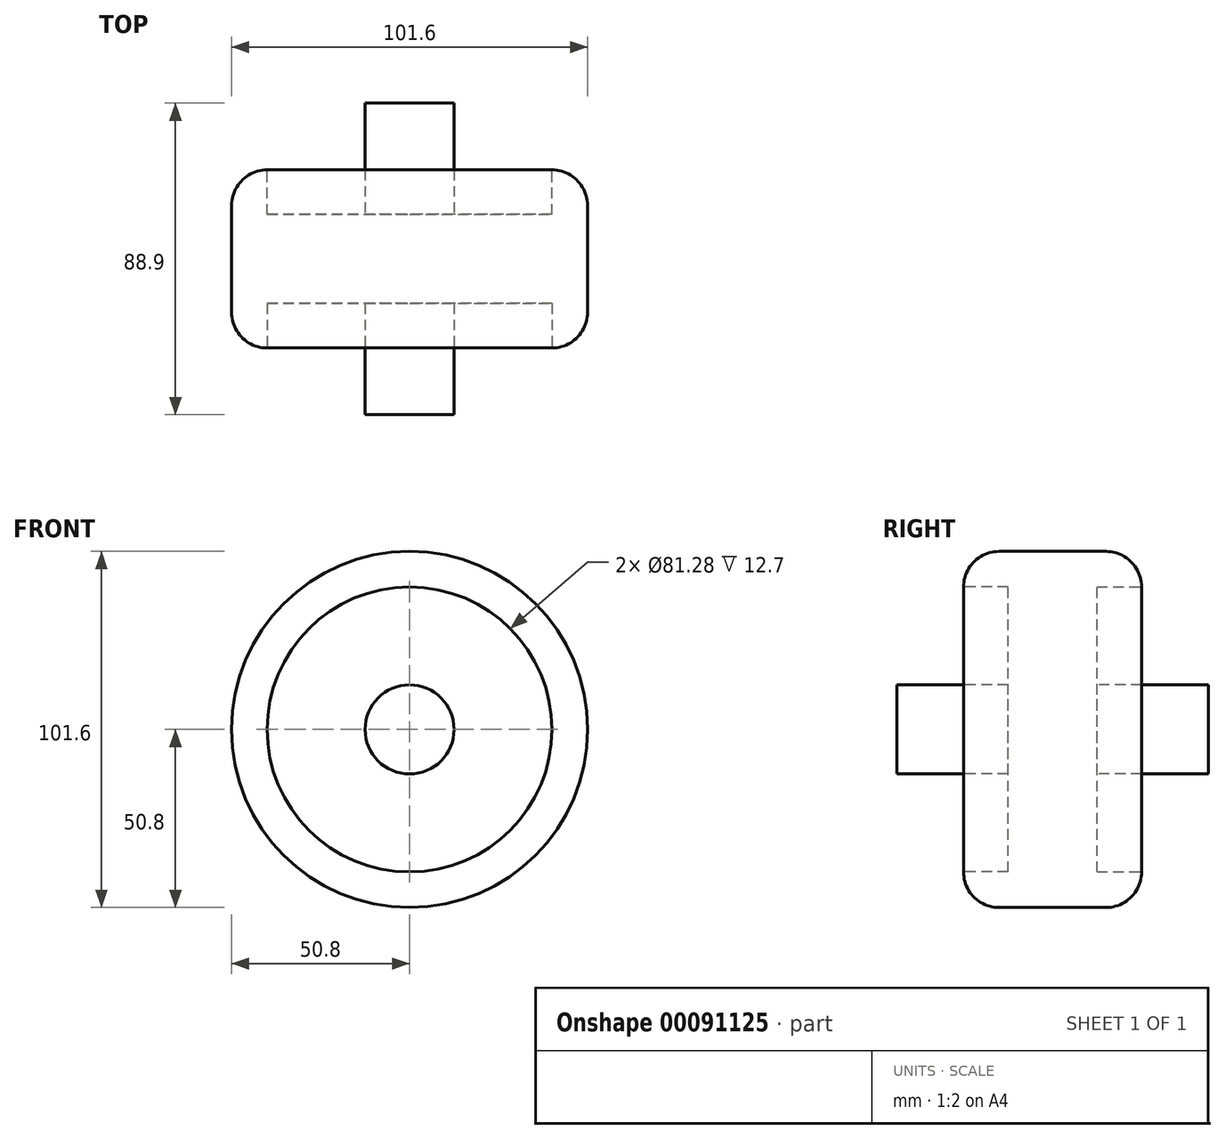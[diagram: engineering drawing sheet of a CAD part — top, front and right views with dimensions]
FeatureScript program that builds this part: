
annotation { "Feature Type Name" : "Feature", "Feature Type Description" : "" }
export const myFeature = defineFeature(function(context is Context, id is Id, definition is map)
    precondition{}
    {
        {
            var Q0;
            Q0=qCreatedBy(makeId("Front.planeOp"),FACE);
            var sketch = newSketch(context, id + "F0", { "sketchPlane" : qUnion([Q0])});
            skCircle(sketch, "E0", {"center": v(0, 0) * mm, "radius": 50.8 * mm});
            skSolve(sketch);
        }
        {
            var Q0;
            Q0=makeQuery(id+"F0.imprint","IMPRINT",FACE,{"disambiguationData":[TD([[makeQuery(id+"F0.imprint","IMPRINT",EDGE,{"derivedFrom":sQuery(id+"F0.wireOp",EDGE,"E0")}),1.0]])]});
            extrude(context, id + "F1", {"entities" : qUnion([Q0]), "endBound" : BoundingType.SYMMETRIC, "depth" : 50.8 * mm});
        }
        {
            var Q0;
            Q0=makeQuery(id+"F1.opExtrude","CAP_EDGE",EDGE,{"disambiguationData":[OSD([sQuery(id+"F0.wireOp",EDGE,"E0")])],"isStart":false});
            var Q1;
            Q1=makeQuery(id+"F1.opExtrude","CAP_EDGE",EDGE,{"disambiguationData":[OSD([sQuery(id+"F0.wireOp",EDGE,"E0")])],"isStart":true});
            fillet(context, id + "F2", {"entities" : qUnion([Q0, Q1]), "radius" : 10.16 * mm, "tangentPropagation" : true, "allowEdgeOverflow" : false});
        }
        {
            var Q0;
            Q0=makeQuery(id+"F1.opExtrude","CAP_FACE",FACE,{"disambiguationData":[OSD([sQuery(id+"F0.wireOp",EDGE,"E0")])],"isStart":false});
            var Q1;
            Q1=makeQuery(id+"F1.opExtrude","CAP_FACE",FACE,{"disambiguationData":[OSD([sQuery(id+"F0.wireOp",EDGE,"E0")])],"isStart":true});
            extrude(context, id + "F3", {"entities" : qUnion([Q0, Q1]), "operationType" : NewBodyOperationType.REMOVE, "depth" : 12.7 * mm});
        }
        {
            var Q0;
            Q0=makeQuery(id+"F1.opExtrude","CAP_FACE",FACE,{"disambiguationData":[OSD([sQuery(id+"F0.wireOp",EDGE,"E0")])],"isStart":false});
            extrude(context, id + "F4", {"entities" : qUnion([Q0]), "operationType" : NewBodyOperationType.REMOVE, "oppositeDirection" : true, "depth" : 12.7 * mm});
        }
        {
            var Q0;
            Q0=qCreatedBy(makeId("Front.planeOp"),FACE);
            var sketch = newSketch(context, id + "F5", { "sketchPlane" : qUnion([Q0])});
            skCircle(sketch, "E1", {"center": v(0, 0) * mm, "radius": 12.7 * mm});
            skSolve(sketch);
        }
        {
            var Q0;
            Q0 = qSketchRegion(id + "F5", true);
            extrude(context, id + "F6", {"entities" : qUnion([Q0]), "operationType" : NewBodyOperationType.ADD, "endBound" : BoundingType.SYMMETRIC, "oppositeDirection" : true, "depth" : 88.9 * mm});
        }
    });
